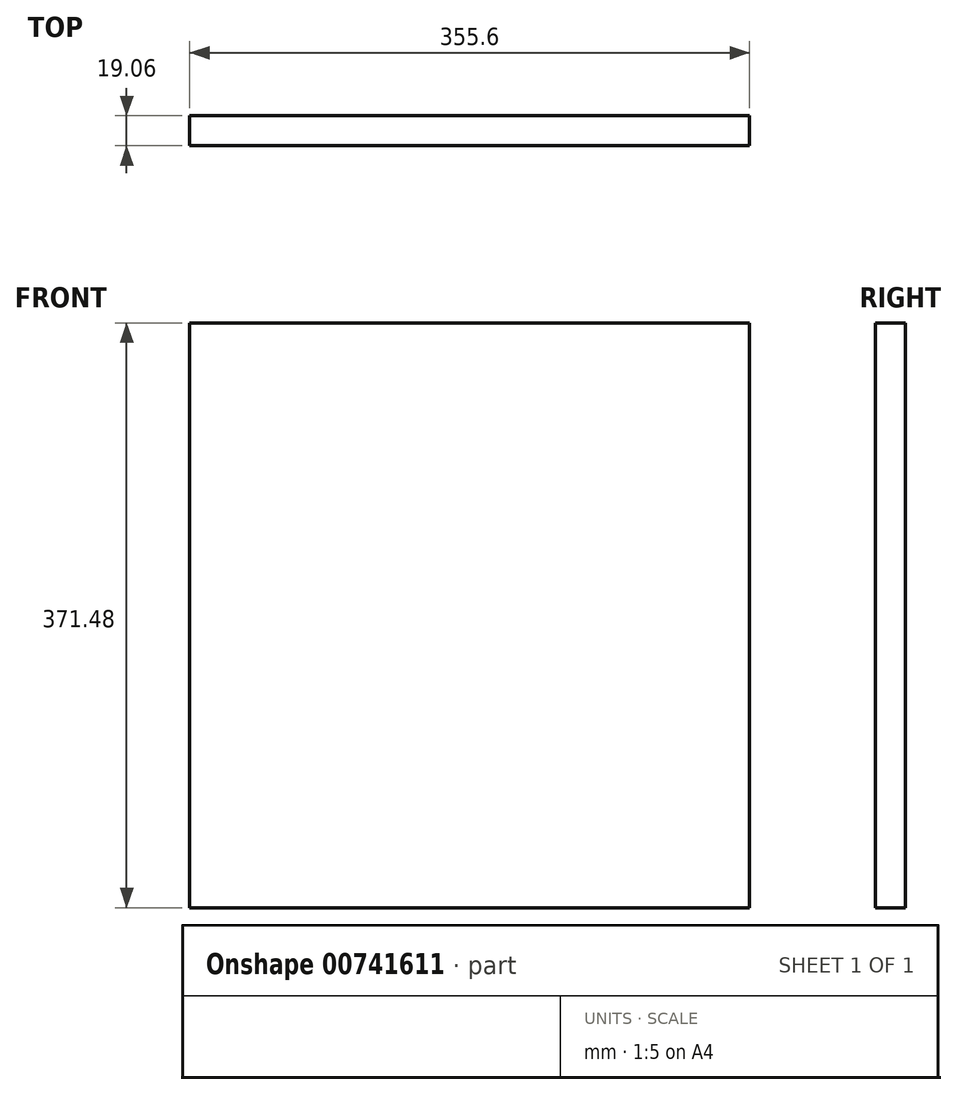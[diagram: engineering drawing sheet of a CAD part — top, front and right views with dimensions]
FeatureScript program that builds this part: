
annotation { "Feature Type Name" : "Feature", "Feature Type Description" : "" }
export const myFeature = defineFeature(function(context is Context, id is Id, definition is map)
    precondition{}
    {
        {
            var Q0;
            Q0=qCreatedBy(makeId("Right.planeOp"),FACE);
            var sketch = newSketch(context, id + "F0", { "sketchPlane" : qUnion([Q0])});
            skLineSegment(sketch, "E0.bottom", {"start": v(9.52, 185.74) * mm, "end": v(-9.53, 185.74) * mm});
            skLineSegment(sketch, "E0.top", {"start": v(9.53, -185.74) * mm, "end": v(-9.52, -185.74) * mm});
            skLineSegment(sketch, "E0.left", {"start": v(9.52, 185.74) * mm, "end": v(9.53, -185.74) * mm});
            skLineSegment(sketch, "E0.right", {"start": v(-9.53, 185.74) * mm, "end": v(-9.52, -185.74) * mm});
            skPoint(sketch, "E0.middle", {"position": v(0, 0) * mm});
            skSolve(sketch);
        }
        {
            var Q0;
            Q0 = qSketchRegion(id + "F0", true);
            extrude(context, id + "F1", {"entities" : qUnion([Q0]), "depth" : 355.6 * mm, "offsetDistance" : 25.4 * mm});
        }
    });
